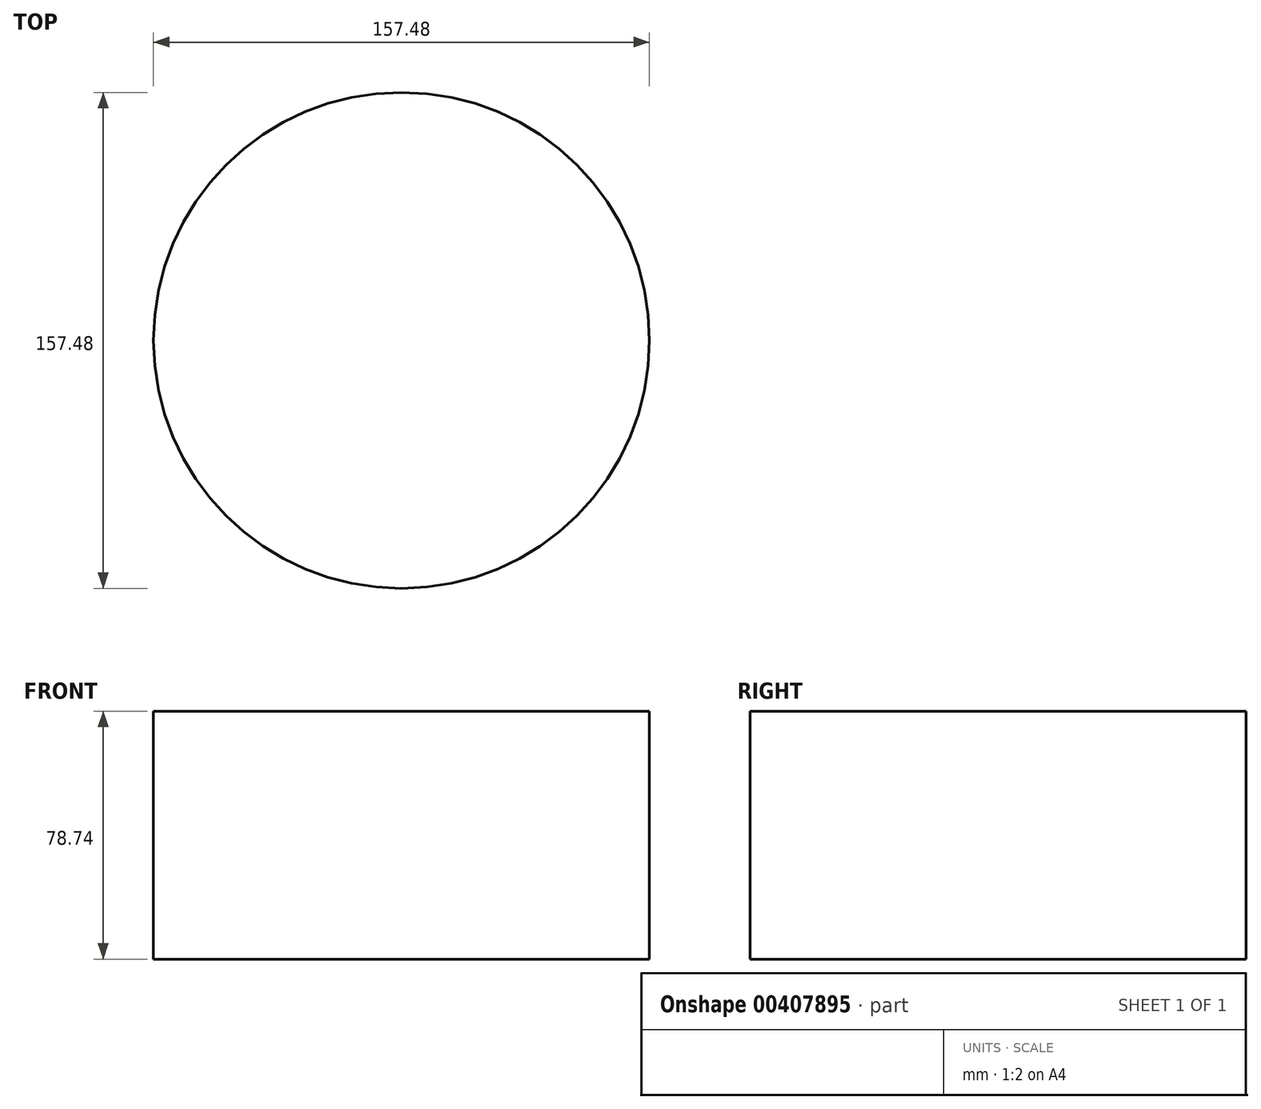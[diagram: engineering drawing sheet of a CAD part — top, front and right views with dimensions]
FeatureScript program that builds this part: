
annotation { "Feature Type Name" : "Feature", "Feature Type Description" : "" }
export const myFeature = defineFeature(function(context is Context, id is Id, definition is map)
    precondition{}
    {
        {
            var Q0;
            Q0=qCreatedBy(makeId("Front.planeOp"),FACE);
            var sketch = newSketch(context, id + "F0", { "sketchPlane" : qUnion([Q0])});
            skLineSegment(sketch, "E0.bottom", {"start": v(0, 0) * mm, "end": v(78.74, 0) * mm});
            skLineSegment(sketch, "E0.top", {"start": v(0, 78.74) * mm, "end": v(78.74, 78.74) * mm});
            skLineSegment(sketch, "E0.left", {"start": v(0, 0) * mm, "end": v(0, 78.74) * mm});
            skLineSegment(sketch, "E0.right", {"start": v(78.74, 0) * mm, "end": v(78.74, 78.74) * mm});
            skSolve(sketch);
        }
        {
            var Q0;
            Q0 = qSketchRegion(id + "F0", true);
            var Q1;
            Q1=sQuery(id+"F0.wireOp",EDGE,"E0.left");
            revolve(context, id + "F1", {"entities" : qUnion([Q0]), "axis" : qUnion([Q1]), "revolveType" : RevolveType.FULL});
        }
    });
